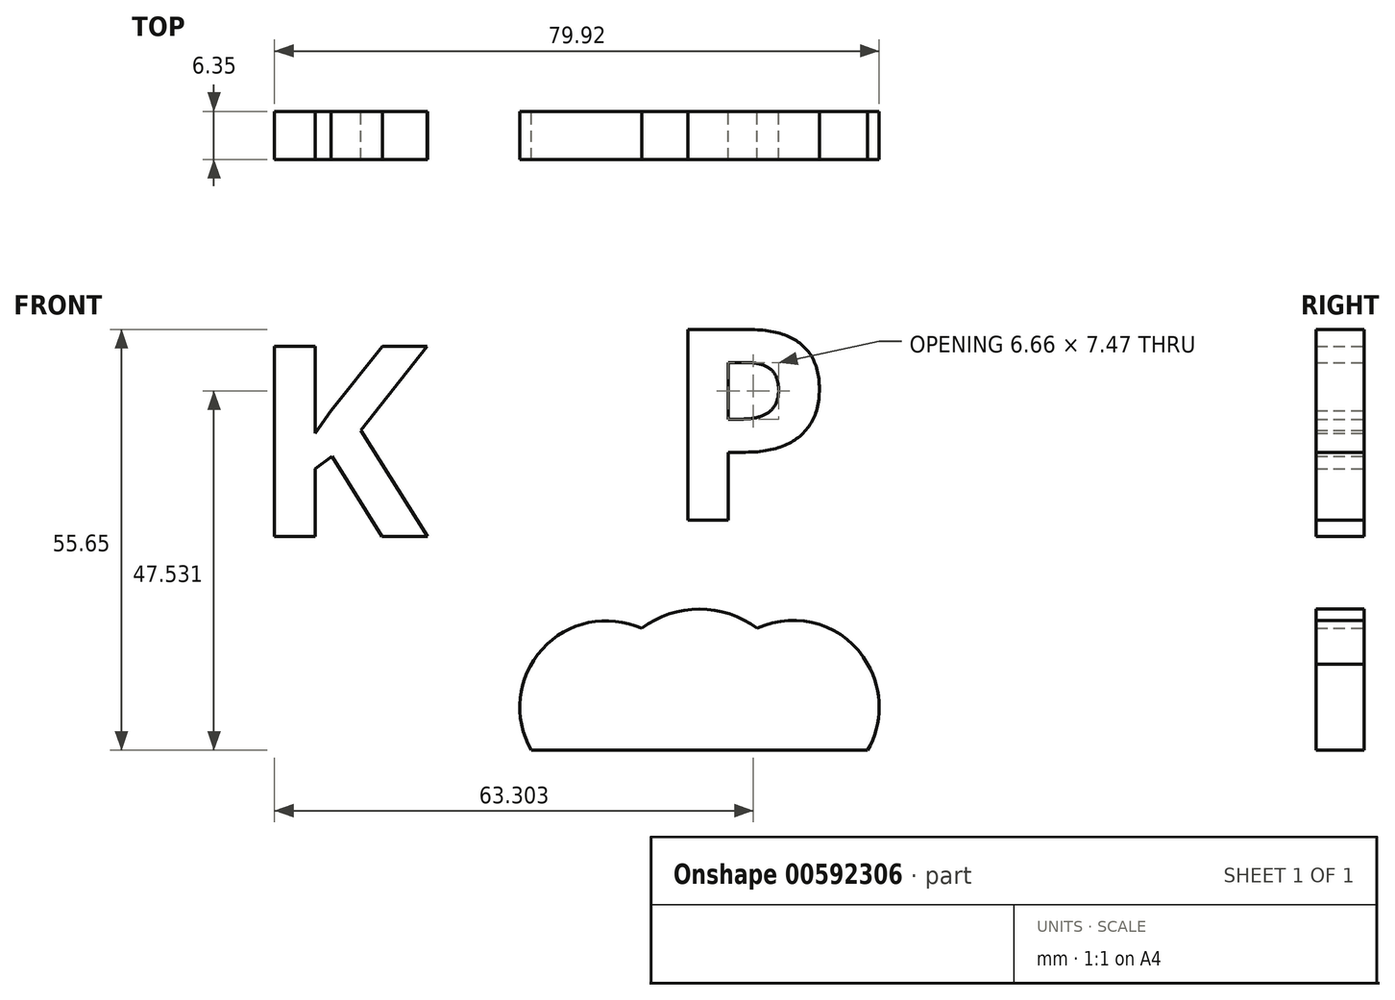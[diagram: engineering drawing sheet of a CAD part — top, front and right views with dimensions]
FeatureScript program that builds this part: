
annotation { "Feature Type Name" : "Feature", "Feature Type Description" : "" }
export const myFeature = defineFeature(function(context is Context, id is Id, definition is map)
    precondition{}
    {
        {
            var Q0;
            Q0=qCreatedBy(makeId("Front.planeOp"),FACE);
            var sketch = newSketch(context, id + "F0", { "sketchPlane" : qUnion([Q0])});
            skLineSegment(sketch, "E0", {"start": v(-22.22, 0) * mm, "end": v(22.22, 0) * mm});
            skArc(sketch, "E1", {"start": v(22.22, 0) * mm, "mid": v(23.75, 5.7) * mm, "end": v(22.22, 11.4) * mm});
            skArc(sketch, "E2.MirrorCS", {"start": v(-22.22, 0) * mm, "mid": v(-23.75, 5.7) * mm, "end": v(-22.22, 11.4) * mm});
            skLineSegment(sketch, "E3.MirrorCS", {"start": v(22.22, 0) * mm, "end": v(-22.22, 0) * mm});
            skArc(sketch, "E4", {"start": v(-11.25, 17.07) * mm, "mid": v(-17.57, 15.85) * mm, "end": v(-22.23, 11.4) * mm});
            skArc(sketch, "E5", {"start": v(-4.52, 14.04) * mm, "mid": v(-7.63, 16.12) * mm, "end": v(-11.25, 17.07) * mm});
            skArc(sketch, "E6", {"start": v(7.63, 16.12) * mm, "mid": v(0, 18.68) * mm, "end": v(-7.63, 16.12) * mm});
            skPoint(sketch, "E6.startSnap0", {"position": v(-7.63, 16.12) * mm});
            skArc(sketch, "E7", {"start": v(10.42, 13.2) * mm, "mid": v(9.14, 14.77) * mm, "end": v(7.63, 16.12) * mm});
            skArc(sketch, "E8", {"start": v(22.23, 11.4) * mm, "mid": v(15.86, 16.65) * mm, "end": v(7.63, 16.12) * mm});
            skText(sketch, "E9", { "text": "P", "fontName": "OpenSans-Bold.ttf"});
            skText(sketch, "E10", { "text": "K", "fontName": "OpenSans-Bold.ttf"});
            const initialGuessF0  = {"E9": [-0.00471, 0.03046, 1, 0, 0.0254], "E10": [-0.05934, 0.02826, 1, 0, 0.0254]};
            skSetInitialGuess(sketch, initialGuessF0);
            skSolve(sketch);
        }
        {
            var Q0;
            Q0 = qSketchRegion(id + "F0", true);
            extrude(context, id + "F1", {"entities" : qUnion([Q0]), "depth" : 6.35 * mm, "offsetDistance" : 25.4 * mm});
        }
        {
            var Q0;
            Q0=sQuery(id+"F0.wireOp",EDGE,"E7");
            var Q1;
            Q1=sQuery(id+"F0.wireOp",EDGE,"E5");
            extrude(context, id + "F2", {"bodyType" : ToolBodyType.SURFACE, "surfaceEntities" : qUnion([Q0, Q1]), "depth" : 6.6 * mm, "offsetDistance" : 25.4 * mm});
        }
    });
